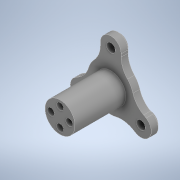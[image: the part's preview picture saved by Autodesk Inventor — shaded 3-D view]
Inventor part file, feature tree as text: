
AUTODESK INVENTOR PART (.ipt)
format: ipt  version: 2022 (Build 260153000, 153)  size: 179,200 bytes
history: mixed  units: in
note: dims shown in document units (in); Inventor stores cm internally (conversion verified against a paired STEP export)
features: extrude x2, sketch x2, chamfer x1, imported_body x1
ambient origin geometry x8: Origin, YZ Plane, XZ Plane, XY Plane, X Axis, Y Axis, Z Axis, Center Point
bodies: Solid1 (imported_parasolid)
feature tree (6):
  extrude  "Extrusion4"  Depth=0.7874in TaperAngle=0.0deg
  extrude  "Extrusion5"  Depth=0.2362in TaperAngle=360.0deg
  sketch  "Sketch4"  dims[d8=0.5118in d9=0.7874in d10=0.0787in d11=0.0in d12=0.0in]
  sketch  "Sketch5"  dims[d14=0.1181in d15=1.5748in d17=360.0deg d19=0.2362in d20=0.0in]
  chamfer  "Chamfer5"  Distance=0.2362in
  imported_body  NMx_Import_Brep_tag  [imported B-rep: ~41 faces, bbox_mm=[31.788121, 26.496463, 26.0]]
